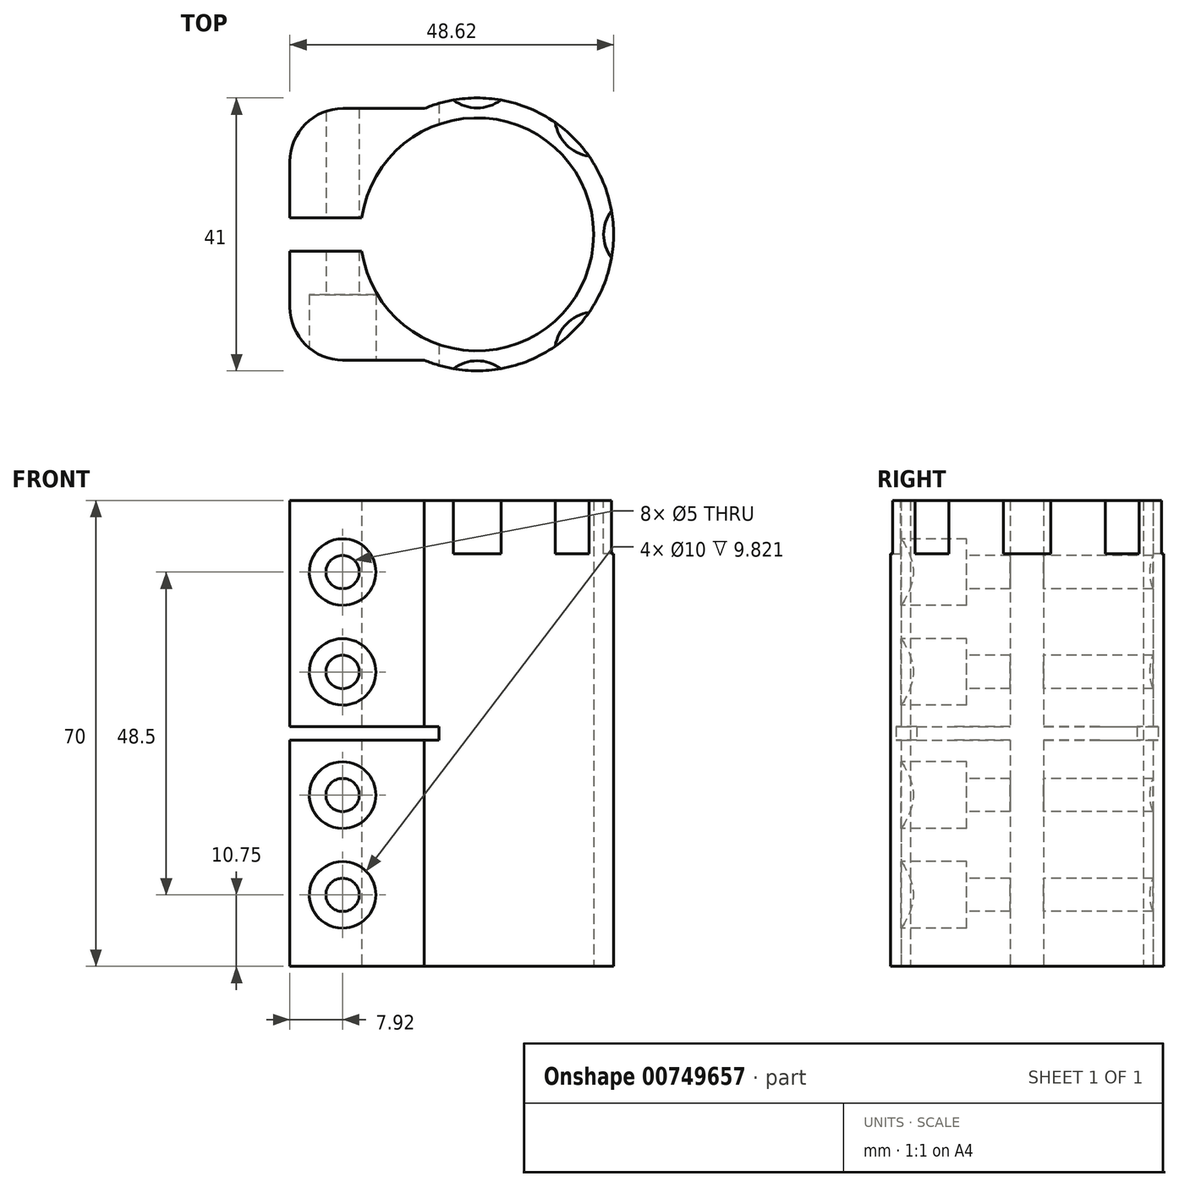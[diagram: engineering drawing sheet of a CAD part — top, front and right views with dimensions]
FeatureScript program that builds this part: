
annotation { "Feature Type Name" : "Feature", "Feature Type Description" : "" }
export const myFeature = defineFeature(function(context is Context, id is Id, definition is map)
    precondition{}
    {
        {
            var Q0;
            Q0=qCreatedBy(makeId("Top.planeOp"),FACE);
            var sketch = newSketch(context, id + "F0", { "sketchPlane" : qUnion([Q0])});
            skArc(sketch, "E0", {"start": v(-7.92, -18.9) * mm, "mid": v(20.5, 0) * mm, "end": v(-7.92, 18.9) * mm});
            skArc(sketch, "E1", {"start": v(-17.32, -2.5) * mm, "mid": v(17.5, 0) * mm, "end": v(-17.32, 2.5) * mm});
            skLineSegment(sketch, "E2", {"start": v(-7.92, 18.9) * mm, "end": v(-20.12, 18.9) * mm});
            skLineSegment(sketch, "E3", {"start": v(-28.12, 10.9) * mm, "end": v(-28.12, 2.5) * mm});
            skLineSegment(sketch, "E4", {"start": v(-28.12, 2.5) * mm, "end": v(-17.32, 2.5) * mm});
            skPoint(sketch, "E5.visualSharp", {"position": v(-28.12, 18.9) * mm});
            skArc(sketch, "E5.filletArc", {"start": v(-20.12, 18.9) * mm, "mid": v(-25.78, 16.57) * mm, "end": v(-28.12, 10.9) * mm});
            skLineSegment(sketch, "E6", {"start": v(0, 0) * mm, "end": v(59.46, 0) * mm, "construction": true});
            skLineSegment(sketch, "E7.MirrorCS", {"start": v(-28.12, -10.9) * mm, "end": v(-28.12, -2.5) * mm});
            skLineSegment(sketch, "E8.MirrorCS", {"start": v(-28.12, -2.5) * mm, "end": v(-17.32, -2.5) * mm});
            skLineSegment(sketch, "E9.MirrorCS", {"start": v(-7.92, -18.9) * mm, "end": v(-20.12, -18.9) * mm});
            skArc(sketch, "E10.MirrorCS", {"start": v(-20.12, -18.9) * mm, "mid": v(-25.78, -16.57) * mm, "end": v(-28.12, -10.9) * mm});
            skSolve(sketch);
        }
        {
            var Q0;
            Q0=qSketchRegion(id+"F0",true);
            extrude(context, id + "F1", {"entities" : qUnion([Q0]), "endBound" : BoundingType.SYMMETRIC, "depth" : 70 * mm, "offsetDistance" : 25 * mm});
        }
        {
            var Q0;
            Q0=makeQuery(id+"F1.opExtrude","SWEPT_FACE",FACE,{"disambiguationData":[OSD([sQuery(id+"F0.wireOp",EDGE,"E9.MirrorCS")])]});
            var sketch = newSketch(context, id + "F2", { "sketchPlane" : qUnion([Q0])});
            skPoint(sketch, "E11", {"position": v(-20.2, -24.25) * mm});
            skPoint(sketch, "E12", {"position": v(-20.2, -9.25) * mm});
            skPoint(sketch, "E13", {"position": v(-20.2, 9.25) * mm});
            skPoint(sketch, "E14", {"position": v(-20.2, 24.25) * mm});
            skSolve(sketch);
        }
        {
            var Q0;
            Q0=sQuery(id+"F2.wireOp",VERTEX,"E11");
            var Q1;
            Q1=sQuery(id+"F2.wireOp",VERTEX,"E12");
            var Q2;
            Q2=sQuery(id+"F2.wireOp",VERTEX,"E13");
            var Q3;
            Q3=sQuery(id+"F2.wireOp",VERTEX,"E14");
            var Q4;
            Q4=makeQuery(id+"F1.opExtrude","SWEPT_BODY",BODY,{"disambiguationData":[OSD([sQuery(id+"F0.wireOp",EDGE,"E0"),sQuery(id+"F0.wireOp",EDGE,"E1"),sQuery(id+"F0.wireOp",EDGE,"E2"),sQuery(id+"F0.wireOp",EDGE,"E3"),sQuery(id+"F0.wireOp",EDGE,"E4"),sQuery(id+"F0.wireOp",EDGE,"E5.filletArc"),sQuery(id+"F0.wireOp",EDGE,"E7.MirrorCS"),sQuery(id+"F0.wireOp",EDGE,"E8.MirrorCS"),sQuery(id+"F0.wireOp",EDGE,"E9.MirrorCS"),sQuery(id+"F0.wireOp",EDGE,"E10.MirrorCS")])]});
            hole(context, id + "F3", {"style" : HoleStyle.C_BORE, "endStyle" : HoleEndStyle.THROUGH, "holeDiameter" : 5 * mm, "cBoreDiameter" : 10 * mm, "cBoreDepth" : 8 * mm, "majorDiameter" : 5 * mm, "isTappedThrough" : true, "tappedDepth" : 12 * mm, "tapClearance" : 3, "locations" : qUnion([Q0, Q1, Q2, Q3]), "scope" : qUnion([Q4])});
        }
        {
            var Q0;
            Q0=qCreatedBy(makeId("Front.planeOp"),FACE);
            var sketch = newSketch(context, id + "F4", { "sketchPlane" : qUnion([Q0])});
            skLineSegment(sketch, "E15.bottom", {"start": v(-28.12, 1) * mm, "end": v(-5.72, 1) * mm});
            skLineSegment(sketch, "E15.top", {"start": v(-28.12, -1) * mm, "end": v(-5.72, -1) * mm});
            skLineSegment(sketch, "E15.left", {"start": v(-28.12, 1) * mm, "end": v(-28.12, -1) * mm});
            skLineSegment(sketch, "E15.right", {"start": v(-5.72, 1) * mm, "end": v(-5.72, -1) * mm});
            skSolve(sketch);
        }
        {
            var Q0;
            Q0=qSketchRegion(id+"F4",true);
            extrude(context, id + "F5", {"entities" : qUnion([Q0]), "operationType" : NewBodyOperationType.REMOVE, "endBound" : BoundingType.SYMMETRIC, "oppositeDirection" : true, "depth" : 50 * mm, "offsetDistance" : 25 * mm});
        }
        {
            var Q0;
            Q0=makeQuery(id+"F1.opExtrude","CAP_FACE",FACE,{"disambiguationData":[OSD([sQuery(id+"F0.wireOp",EDGE,"E0"),sQuery(id+"F0.wireOp",EDGE,"E1"),sQuery(id+"F0.wireOp",EDGE,"E2"),sQuery(id+"F0.wireOp",EDGE,"E3"),sQuery(id+"F0.wireOp",EDGE,"E4"),sQuery(id+"F0.wireOp",EDGE,"E5.filletArc"),sQuery(id+"F0.wireOp",EDGE,"E7.MirrorCS"),sQuery(id+"F0.wireOp",EDGE,"E8.MirrorCS"),sQuery(id+"F0.wireOp",EDGE,"E9.MirrorCS"),sQuery(id+"F0.wireOp",EDGE,"E10.MirrorCS")])],"isStart":false});
            var sketch = newSketch(context, id + "F6", { "sketchPlane" : qUnion([Q0])});
            skCircle(sketch, "E16", {"center": v(0, -25) * mm, "radius": 6 * mm});
            skCircle(sketch, "E17.1.0", {"center": v(17.68, -17.68) * mm, "radius": 6 * mm});
            skCircle(sketch, "E17.2.0", {"center": v(25, 0) * mm, "radius": 6 * mm});
            skCircle(sketch, "E17.3.0", {"center": v(17.68, 17.68) * mm, "radius": 6 * mm});
            skCircle(sketch, "E17.4.0", {"center": v(0, 25) * mm, "radius": 6 * mm});
            skPoint(sketch, "E17.center", {"position": v(0, 0) * mm});
            skLineSegment(sketch, "E17.anchor1", {"start": v(0, 0) * mm, "end": v(0, -25) * mm, "construction": true});
            skLineSegment(sketch, "E17.anchor2", {"start": v(0, 0) * mm, "end": v(0, 25) * mm, "construction": true});
            skSolve(sketch);
        }
        {
            var Q0;
            Q0=qSketchRegion(id+"F6",true);
            extrude(context, id + "F7", {"entities" : qUnion([Q0]), "operationType" : NewBodyOperationType.REMOVE, "oppositeDirection" : true, "depth" : 8 * mm, "offsetDistance" : 25 * mm});
        }
    });
